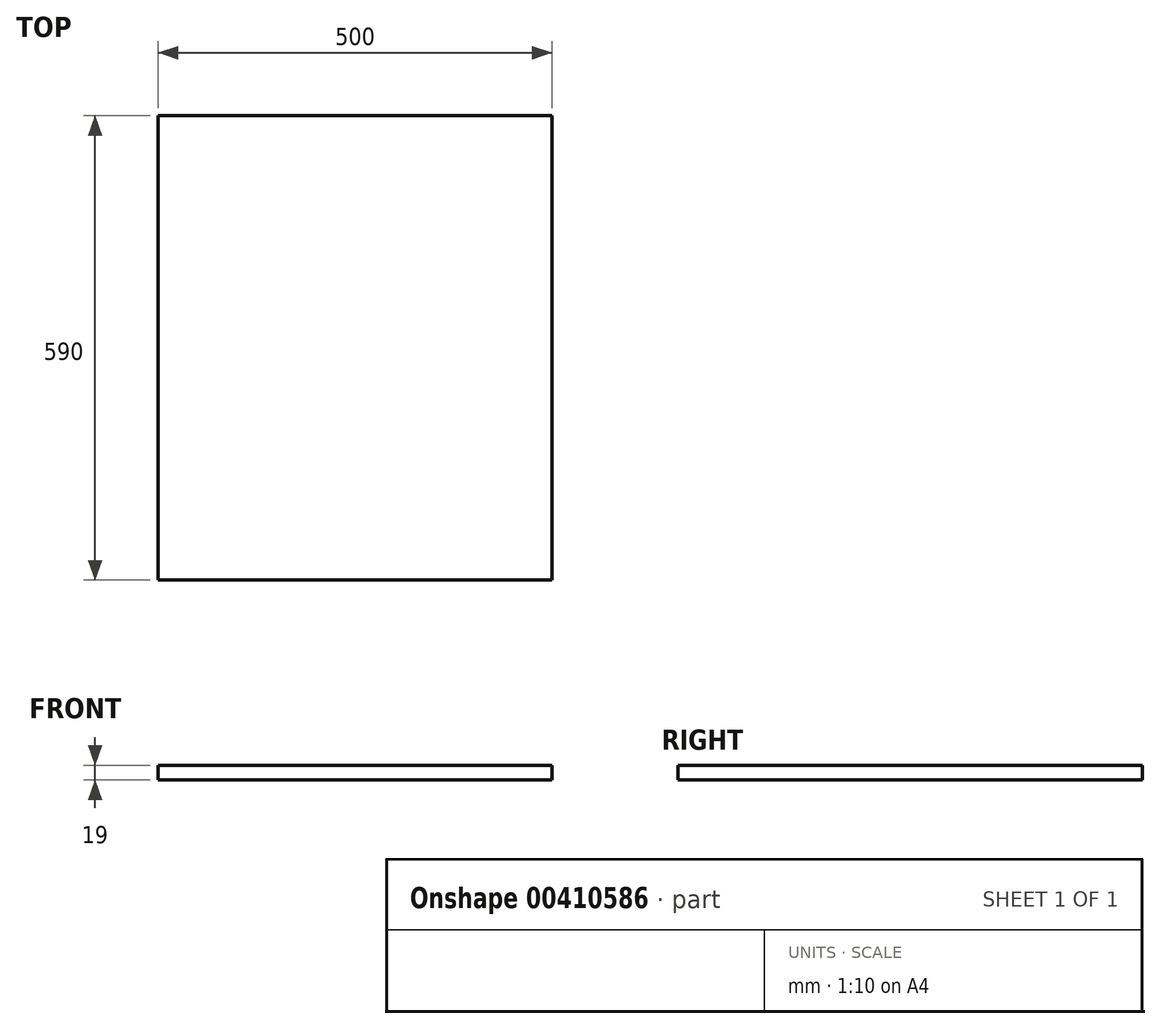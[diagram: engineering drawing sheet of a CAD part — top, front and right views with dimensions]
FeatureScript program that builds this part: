
annotation { "Feature Type Name" : "Feature", "Feature Type Description" : "" }
export const myFeature = defineFeature(function(context is Context, id is Id, definition is map)
    precondition{}
    {
        {
            var Q0;
            Q0=qCreatedBy(makeId("Top.planeOp"),FACE);
            var sketch = newSketch(context, id + "F0", { "sketchPlane" : qUnion([Q0])});
            skLineSegment(sketch, "E0.bottom", {"start": v(-250, 295) * mm, "end": v(250, 295) * mm});
            skLineSegment(sketch, "E0.top", {"start": v(-250, -295) * mm, "end": v(250, -295) * mm});
            skLineSegment(sketch, "E0.left", {"start": v(-250, 295) * mm, "end": v(-250, -295) * mm});
            skLineSegment(sketch, "E0.right", {"start": v(250, 295) * mm, "end": v(250, -295) * mm});
            skPoint(sketch, "E0.middle", {"position": v(0, 0) * mm});
            skSolve(sketch);
        }
        {
            var Q0;
            Q0=makeQuery(id+"F0.imprint","IMPRINT",FACE,{"disambiguationData":[TD([[makeQuery(id+"F0.imprint","IMPRINT",EDGE,{"derivedFrom":sQuery(id+"F0.wireOp",EDGE,"E0.bottom")}),-1.0]])]});
            extrude(context, id + "F1", {"entities" : qUnion([Q0]), "depth" : 19 * mm});
        }
    });
